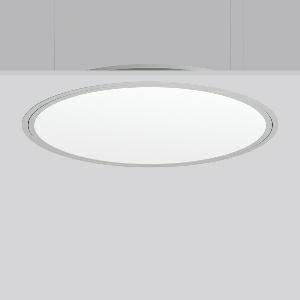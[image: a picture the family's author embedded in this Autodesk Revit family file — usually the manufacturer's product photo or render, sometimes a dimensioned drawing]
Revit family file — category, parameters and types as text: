
# Revit family: triona_round_e_312387_004_2_12_c8a5
name_source: partatom
category: Lighting Fixtures
units: mm (PartAtom-declared; Revit-internal decimal feet)

## family parameters
Cut with Voids When Loaded = No
Host = Face
Light Source = No
Part Type = Normal
Room Calculation Point = No
Round Connector Dimension = Use Diameter
Shared = No

## types (1)
- TuneableWhite 846 (1 x LED Modul 846, 4800 lm, 4600)
    Apparent Load = 49 VA
    CIE Flux Codes = 50 80 96 100 100
    Color Rendering = 80
    Color Temperature = 4600
    Default Elevation = 1800 mm
    Description = Series: TRIONA round
Decorative round LED recessed surface luminaire. Cover made of sheet steel, powder-coated. Frame made of aluminium, powder-coated. Recessed ring: aluminium extrusion profile, powder coated. Light emission through a diffuser: plastic, opal. Lightguide and diffuser made of non-yellowing plastic (PMMA). Lateral light emission (RZB SIDELITE technology) for above-average homogeneous light distribution. Tunable white versions, dynamically adjustable from 2700 K to 6500 K. Suitable for installation in cavity ceilings. Tool-free mounting system thanks to the rocker arm mechanism (patent pending). Electronic ballast included. Very easy installation thanks to Plug+Play connection. Ideal for use as part of the Human Centric Lighting concept in connection with RZB light management systems. 
Colour: silver, matt (approx. RAL 9006)
Diameter: 889 mm
Height: 2 mm
Cut-out diameter: 866 mm
Recess height: 100 mm
Luminaire: recess height: 89 mm
Lamp: LED
Socket: without socket
Colour temperature: 2700K - 6500K
Colour rendering index (CRI): 80
System power: 49 W
Rated luminous flux: 4800 lm
Luminous efficiency: 98 lm/W
System power 2: 51 W
Rated luminous flux 2: 4550 lm
Luminous efficiency 2: 89 lm/W
System power 3: 51 W
Rated luminous flux 3: 4650 lm
Luminous efficiency 3: 91 lm/W
Control gear: Converter, dimmable, DALI
Protection class: I
Type of protection: IP 40
    Height = 0 mm  [stored 0 ft]
    Lamp = 1 x LED Modul 846
    Lamp Light Flux = 4800 lm
    Lamp count = 1
    Length = 889 mm
    Lifetime = 50000 h
    Luminous efficacy = 98 lm/W
    Manufacturer = RZB
    ModVariant = No
    Model = 312387.004.2.12
    Mounting Place = Ceiling
    Mounting Type = Recessed
    Number of Poles = 1
    OnlyDefault = Yes
    Power Factor = 1
    Product Name = TRIONA round E
    Product group = Recessed modular luminaires
    ProductGroupID = 406
    Protection Class = Protection class I
    Protection Degree = IP 20
    RLX_Detail_Level = 1
    RLX_Emergency_Light_Flux = 0 lm
    RLX_Emergency_Type = 0
    RLX_Emergency_Type_DB = No
    RlxData = <blob elided: 39953 chars, md5=3e8083b3>
    Socket = socket
    Standby Power = 0 W
    System Light Flux = 4800 lm
    System Power = 49 W
    Type Comments = TuneableWhite 846
    Type Image = 312387.004.12.jpg
    URL = http://relux.com
    VarID = tuneablewhite_846
    Voltage = 230 V
    Voltage Range = 220-240 V
    Weight = 0.00 kg
    Width = 0 mm  [stored 0 ft]

note: [stored X ft] marks values corroborated as IEEE doubles in the binary element streams (Revit-internal decimal feet)

## geometry (parser evidence)
native form markers: Blend x4, Sweep x10
no freeform markers — native parametric forms only
